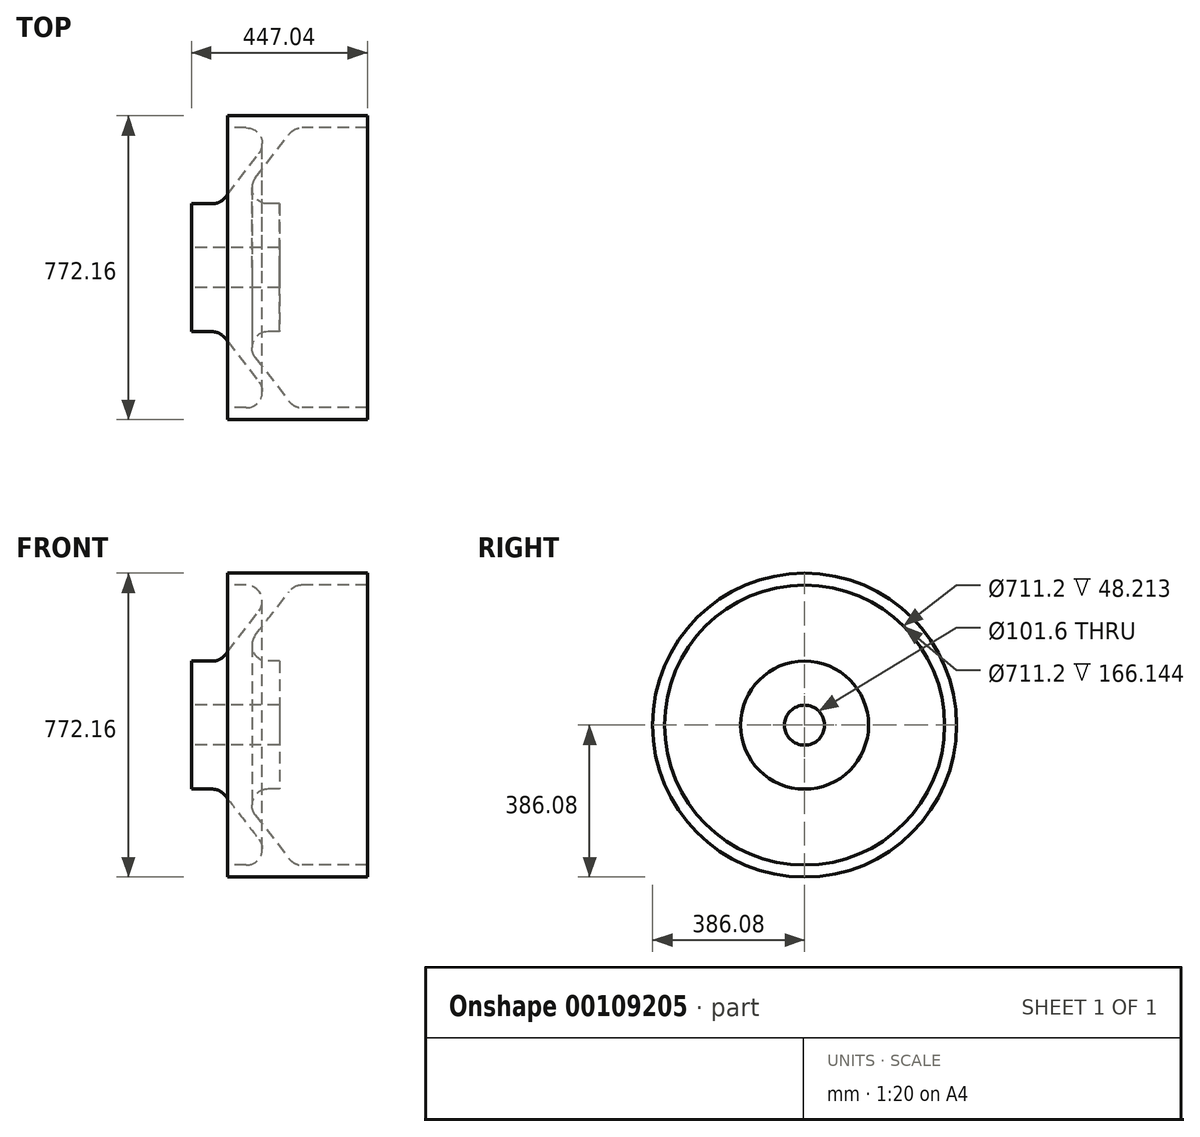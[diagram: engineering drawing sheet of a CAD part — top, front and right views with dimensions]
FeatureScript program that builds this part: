
annotation { "Feature Type Name" : "Feature", "Feature Type Description" : "" }
export const myFeature = defineFeature(function(context is Context, id is Id, definition is map)
    precondition{}
    {
        {
            var Q0;
            Q0=qCreatedBy(makeId("Front.planeOp"),FACE);
            var sketch = newSketch(context, id + "F0", { "sketchPlane" : qUnion([Q0])});
            skLineSegment(sketch, "E0", {"start": v(-194.22, 0) * mm, "end": v(183.85, 0) * mm, "construction": true});
            skLineSegment(sketch, "E1.0", {"start": v(-194.22, 241.3) * mm, "end": v(183.85, 241.3) * mm, "construction": true});
            skLineSegment(sketch, "E2.0", {"start": v(-194.22, 222.25) * mm, "end": v(183.85, 222.25) * mm, "construction": true});
            skLineSegment(sketch, "E3", {"start": v(0, 0) * mm, "end": v(0, 338.49) * mm, "construction": true});
            skLineSegment(sketch, "E4.0", {"start": v(111.13, 0) * mm, "end": v(111.13, 338.49) * mm, "construction": true});
            skLineSegment(sketch, "E5.bottom", {"start": v(111.13, 241.3) * mm, "end": v(-111.12, 241.3) * mm});
            skLineSegment(sketch, "E5.top", {"start": v(111.13, 222.25) * mm, "end": v(-111.12, 222.25) * mm});
            skLineSegment(sketch, "E5.left", {"start": v(111.13, 241.3) * mm, "end": v(111.13, 222.25) * mm});
            skLineSegment(sketch, "E5.right", {"start": v(-111.13, 241.3) * mm, "end": v(-111.13, 222.25) * mm});
            skLineSegment(sketch, "E6.0", {"start": v(-28.58, 0) * mm, "end": v(-28.58, 338.49) * mm, "construction": true});
            skLineSegment(sketch, "E7.0", {"start": v(-168.28, 0) * mm, "end": v(-168.28, 338.49) * mm, "construction": true});
            skLineSegment(sketch, "E8.0", {"start": v(-194.22, 101.6) * mm, "end": v(183.85, 101.6) * mm, "construction": true});
            skLineSegment(sketch, "E9.0", {"start": v(-194.22, 31.75) * mm, "end": v(183.85, 31.75) * mm, "construction": true});
            skLineSegment(sketch, "E10.bottom", {"start": v(-168.28, 101.6) * mm, "end": v(-28.58, 101.6) * mm});
            skLineSegment(sketch, "E10.top", {"start": v(-168.28, 31.75) * mm, "end": v(-28.58, 31.75) * mm});
            skLineSegment(sketch, "E10.left", {"start": v(-168.28, 101.6) * mm, "end": v(-168.28, 31.75) * mm});
            skLineSegment(sketch, "E10.right", {"start": v(-28.58, 101.6) * mm, "end": v(-28.58, 31.75) * mm});
            skLineSegment(sketch, "E11", {"start": v(-98.43, 101.6) * mm, "end": v(-5.19, 222.25) * mm});
            skLineSegment(sketch, "E12.0", {"start": v(-122.5, 101.6) * mm, "end": v(-20.26, 233.9) * mm});
            skSolve(sketch);
        }
        {
            var Q0;
            Q0=qSketchRegion(id+"F0",true);
            var Q1;
            Q1=sQuery(id+"F0.wireOp",EDGE,"E0");
            revolve(context, id + "F1", {"entities" : qUnion([Q0]), "axis" : qUnion([Q1]), "revolveType" : RevolveType.FULL});
        }
        {
            var Q0;
            Q0=makeQuery(id+"F1.opRevolve","SWEPT_FACE",FACE,{"disambiguationData":[OSD([sQuery(id+"F0.wireOp",EDGE,"E11")])]});
            var Q1;
            Q1=makeQuery(id+"F1.opRevolve","SWEPT_FACE",FACE,{"disambiguationData":[OSD([sQuery(id+"F0.wireOp",EDGE,"E12.0")])]});
            fillet(context, id + "F2", {"entities" : qUnion([Q0, Q1]), "radius" : 25.4 * mm, "tangentPropagation" : true, "allowEdgeOverflow" : false});
        }
        {
            var Q0;
            Q0=makeQuery(id+"F1.opRevolve","SWEPT_BODY",BODY,{"disambiguationData":[OSD([sQuery(id+"F0.wireOp",EDGE,"E5.bottom"),sQuery(id+"F0.wireOp",EDGE,"E5.top"),sQuery(id+"F0.wireOp",EDGE,"E5.left"),sQuery(id+"F0.wireOp",EDGE,"E5.right"),sQuery(id+"F0.wireOp",EDGE,"E10.bottom"),sQuery(id+"F0.wireOp",EDGE,"E10.top"),sQuery(id+"F0.wireOp",EDGE,"E10.left"),sQuery(id+"F0.wireOp",EDGE,"E10.right"),sQuery(id+"F0.wireOp",EDGE,"E11"),sQuery(id+"F0.wireOp",EDGE,"E12.0")])]});
            var Q1;
            Q1=qCreatedBy(makeId("Origin.pointOp"),VERTEX);
            transform(context, id + "F3", {"entities" : qUnion([Q0]), "transformType" : TransformType.SCALE_UNIFORMLY, "scale" : 1.6, "scalePoint" : qUnion([Q1]), "makeCopy" : false});
        }
    });
